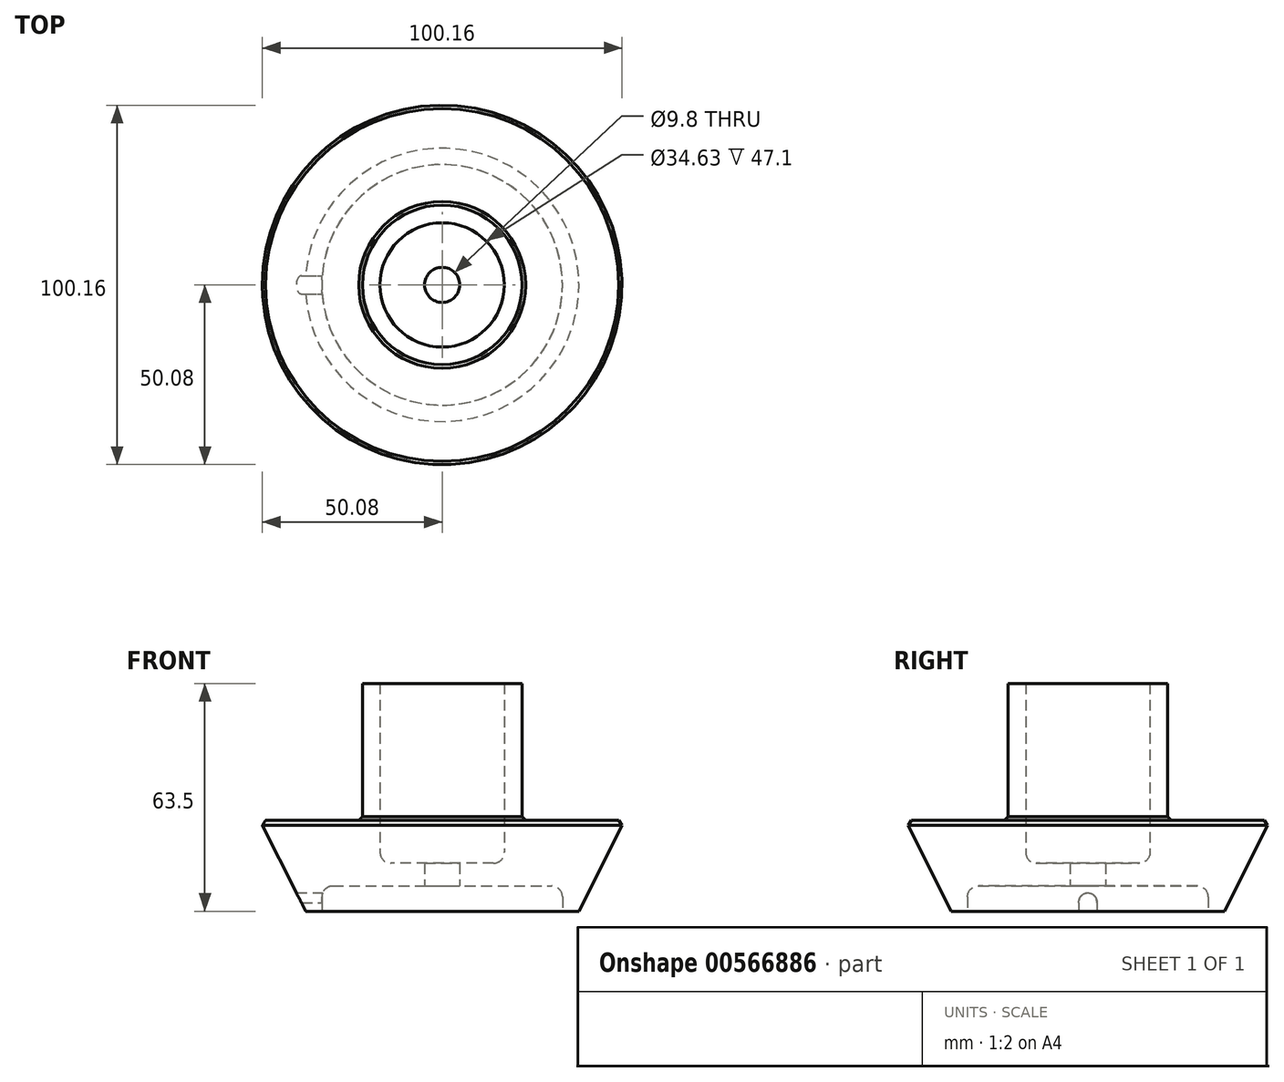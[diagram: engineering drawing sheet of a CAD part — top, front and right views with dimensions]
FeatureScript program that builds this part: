
annotation { "Feature Type Name" : "Feature", "Feature Type Description" : "" }
export const myFeature = defineFeature(function(context is Context, id is Id, definition is map)
    precondition{}
    {
        {
            var Q0;
            Q0=qCreatedBy(makeId("Top.planeOp"),FACE);
            var sketch = newSketch(context, id + "F0", { "sketchPlane" : qUnion([Q0])});
            skCircle(sketch, "E0", {"center": v(0, 0) * mm, "radius": 22.23 * mm});
            skCircle(sketch, "E1", {"center": v(0, 0) * mm, "radius": 17.32 * mm});
            skSolve(sketch);
        }
        {
            var Q0;
            Q0 = qSketchRegion(id + "F0", true);
            var Q1;
            Q1 = qSketchRegion(id + "F5", true);
            extrude(context, id + "F1", {"entities" : qUnion([Q0, Q1]), "depth" : 63.5 * mm, "offsetDistance" : 25.4 * mm});
        }
        {
            var Q0;
            Q0=qCreatedBy(makeId("Right.planeOp"),FACE);
            var sketch = newSketch(context, id + "F2", { "sketchPlane" : qUnion([Q0])});
            skLineSegment(sketch, "E2", {"start": v(0, 0) * mm, "end": v(-38.1, 0) * mm});
            skLineSegment(sketch, "E3", {"start": v(0, 0) * mm, "end": v(0, 25.4) * mm});
            skLineSegment(sketch, "E4", {"start": v(0, 25.4) * mm, "end": v(-50.8, 25.4) * mm});
            skLineSegment(sketch, "E5", {"start": v(-50.8, 25.4) * mm, "end": v(-38.1, 0) * mm});
            skLineSegment(sketch, "E6", {"start": v(0, 25.4) * mm, "end": v(-17.32, 25.4) * mm});
            skSolve(sketch);
        }
        {
            var Q0;
            Q0 = qSketchRegion(id + "F2", true);
            var Q1;
            Q1=sQuery(id+"F2.wireOp",EDGE,"E3");
            revolve(context, id + "F3", {"operationType" : NewBodyOperationType.ADD, "entities" : qUnion([Q0]), "axis" : qUnion([Q1]), "revolveType" : RevolveType.FULL});
        }
        {
            var Q0;
            Q0=makeQuery(id+"F3.opRevolve","SWEPT_EDGE",EDGE,{"disambiguationData":[OSD([sQuery(id+"F2.wireOp",EDGE,"E4"),sQuery(id+"F2.wireOp",EDGE,"E5")])]});
            chamfer(context, id + "F4", {"entities" : qUnion([Q0]), "width" : 1 * mm, "tangentPropagation" : true});
        }
        {
            var Q0;
            Q0=qCreatedBy(makeId("Top.planeOp"),FACE);
            var sketch = newSketch(context, id + "F5", { "sketchPlane" : qUnion([Q0])});
            skCircle(sketch, "E7", {"center": v(0, 0) * mm, "radius": 4.9 * mm});
            skSolve(sketch);
        }
        {
            var Q0;
            Q0 = qSketchRegion(id + "F5", true);
            var Q1;
            Q1=makeQuery(id+"F3.boolean.opBoolean","SPLIT",FACE,{"disambiguationData":[TD([makeQuery(id+"F1.opExtrude","SWEPT_FACE",FACE,{"disambiguationData":[OSD([sQuery(id+"F0.wireOp",EDGE,"E0")])]})])],"derivedFrom":makeQuery(id+"F3.opRevolve","SWEPT_FACE",FACE,{"disambiguationData":[OSD([sQuery(id+"F2.wireOp",EDGE,"E4")])]})});
            extrude(context, id + "F6", {"entities" : qUnion([Q0, Q1]), "operationType" : NewBodyOperationType.REMOVE, "oppositeDirection" : true, "depth" : -40 * mm, "offsetDistance" : 25 * mm});
        }
        {
            var Q0;
            Q0 = qSketchRegion(id + "F5", true);
            extrude(context, id + "F7", {"entities" : qUnion([Q0]), "operationType" : NewBodyOperationType.REMOVE, "endBound" : BoundingType.THROUGH_ALL, "depth" : 30 * mm, "offsetDistance" : 25 * mm, "hasSecondDirection" : true, "secondDirectionOppositeDirection" : true, "secondDirectionDepth" : 30 * mm});
        }
        {
            var Q0;
            Q0=makeQuery(id+"F3.boolean.opBoolean","SPLIT",FACE,{"disambiguationData":[TD([makeQuery(id+"F1.opExtrude","SWEPT_FACE",FACE,{"disambiguationData":[OSD([sQuery(id+"F0.wireOp",EDGE,"E0")])]})])],"derivedFrom":makeQuery(id+"F3.opRevolve","SWEPT_FACE",FACE,{"disambiguationData":[OSD([sQuery(id+"F2.wireOp",EDGE,"E4")])]})});
            var sketch = newSketch(context, id + "F8", { "sketchPlane" : qUnion([Q0])});
            skCircle(sketch, "E8", {"center": v(0, 0) * mm, "radius": 17.32 * mm});
            skSolve(sketch);
        }
        {
            var Q0;
            Q0 = qSketchRegion(id + "F8", true);
            extrude(context, id + "F9", {"entities" : qUnion([Q0]), "operationType" : NewBodyOperationType.REMOVE, "oppositeDirection" : true, "depth" : 12 * mm, "offsetDistance" : 25 * mm});
        }
        {
            var Q0;
            Q0=makeQuery(id+"F9.boolean.opBoolean","COPY",EDGE,{"derivedFrom":makeQuery(id+"F9.opExtrude","CAP_EDGE",EDGE,{"disambiguationData":[OSD([sQuery(id+"F8.wireOp",EDGE,"E8")])],"isStart":false})});
            fillet(context, id + "F10", {"entities" : qUnion([Q0]), "radius" : 3 * mm, "tangentPropagation" : true, "allowEdgeOverflow" : false});
        }
        {
            var Q0;
            Q0=makeQuery(id+"F3.boolean.opBoolean","MERGE",FACE,{"derivedFrom":[makeQuery(id+"F1.opExtrude","CAP_FACE",FACE,{"disambiguationData":[OSD([sQuery(id+"F0.wireOp",EDGE,"E0"),sQuery(id+"F0.wireOp",EDGE,"E1")])],"isStart":true}),makeQuery(id+"F3.opRevolve","SWEPT_FACE",FACE,{"disambiguationData":[OSD([sQuery(id+"F2.wireOp",EDGE,"E2")])]})]});
            var sketch = newSketch(context, id + "F11", { "sketchPlane" : qUnion([Q0])});
            skCircle(sketch, "E9", {"center": v(0, 0) * mm, "radius": 33.53 * mm});
            skSolve(sketch);
        }
        {
            var Q0;
            Q0 = qSketchRegion(id + "F11", true);
            extrude(context, id + "F12", {"entities" : qUnion([Q0]), "operationType" : NewBodyOperationType.REMOVE, "oppositeDirection" : true, "depth" : 7 * mm, "offsetDistance" : 25 * mm});
        }
        {
            var Q0;
            Q0=makeQuery(id+"F12.boolean.opBoolean","COPY",EDGE,{"derivedFrom":makeQuery(id+"F12.opExtrude","CAP_EDGE",EDGE,{"disambiguationData":[OSD([sQuery(id+"F11.wireOp",EDGE,"E9")])],"isStart":false})});
            fillet(context, id + "F13", {"entities" : qUnion([Q0]), "radius" : 3 * mm, "tangentPropagation" : true, "allowEdgeOverflow" : false});
        }
        {
            var Q0;
            Q0=qCreatedBy(makeId("Right.planeOp"),FACE);
            var sketch = newSketch(context, id + "F14", { "sketchPlane" : qUnion([Q0])});
            skLineSegment(sketch, "E10.bottom", {"start": v(-2.5, 0) * mm, "end": v(2.5, 0) * mm});
            skLineSegment(sketch, "E10.top", {"start": v(-2.5, -4.87) * mm, "end": v(2.5, -4.87) * mm});
            skLineSegment(sketch, "E10.left", {"start": v(-2.5, 0) * mm, "end": v(-2.5, -4.87) * mm});
            skLineSegment(sketch, "E10.right", {"start": v(2.5, 0) * mm, "end": v(2.5, -4.87) * mm});
            skCircle(sketch, "E11", {"center": v(0, 2.62) * mm, "radius": 2.5 * mm});
            skLineSegment(sketch, "E12", {"start": v(-2.49, 2.9) * mm, "end": v(-2.5, 0) * mm});
            skLineSegment(sketch, "E13", {"start": v(2.5, 2.82) * mm, "end": v(2.5, 0) * mm});
            skSolve(sketch);
        }
        {
            var Q0;
            Q0 = qSketchRegion(id + "F14", true);
            extrude(context, id + "F15", {"entities" : qUnion([Q0]), "operationType" : NewBodyOperationType.REMOVE, "endBound" : BoundingType.THROUGH_ALL, "oppositeDirection" : true, "depth" : 25 * mm, "offsetDistance" : 25 * mm});
        }
        {
            var Q0;
            Q0=makeQuery(id+"F3.boolean.opBoolean","INTERSECT",EDGE,{"derivedFrom":[makeQuery(id+"F1.opExtrude","SWEPT_FACE",FACE,{"disambiguationData":[OSD([sQuery(id+"F0.wireOp",EDGE,"E0")])]}),makeQuery(id+"F3.opRevolve","SWEPT_FACE",FACE,{"disambiguationData":[OSD([sQuery(id+"F2.wireOp",EDGE,"E4"),sQuery(id+"F2.wireOp",EDGE,"E6")])]})]});
            chamfer(context, id + "F16", {"entities" : qUnion([Q0]), "width" : 1 * mm, "tangentPropagation" : true});
        }
    });
